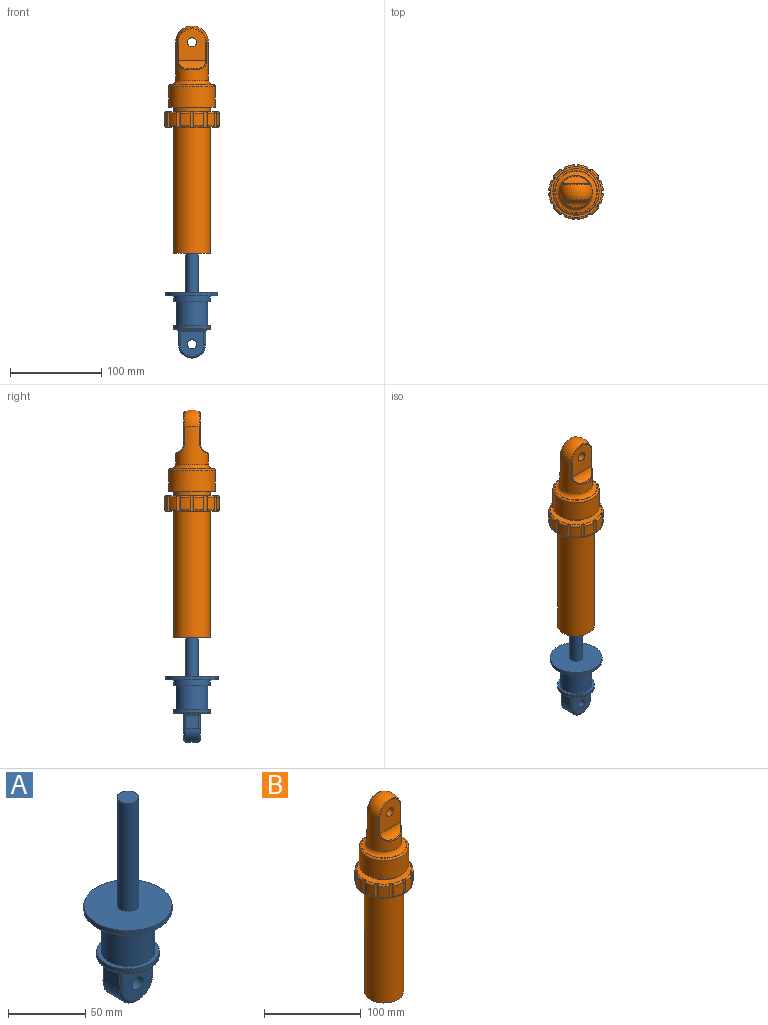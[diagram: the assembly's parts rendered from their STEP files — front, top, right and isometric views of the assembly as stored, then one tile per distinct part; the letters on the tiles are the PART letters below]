
ASSEMBLY  parts=2 mates=1
PART A: 32 faces, bbox 57.1x57.1x158.7 mm
  f0: plane 38.37x38.37mm, normal (0,0,-1), area 420.3mm2, adj f18,f21,f22,f25,f26,f28,f29,f30
  f1: plane 57.1x57.1mm, normal (0,0,1), area 2407mm2, adj f2,f16
  f2: cylinder r=28.55mm len=57.1mm, axis (0,0,-1), area 645.3mm2, adj f1,f3
  f3: plane 57.1x57.1mm, normal (0,0,-1), area 1281.1mm2, adj f2,f4
  f4: cylinder r=20.18mm len=40.37mm, axis (0,0,-1), area 815.9mm2, adj f3,f5
  f5: plane 40.37x40.37mm, normal (0,0,-1), area 322.7mm2, adj f4,f6
  f6: cylinder r=17.46mm len=34.91mm, axis (0,0,-1), area 2870.3mm2, adj f5,f7
  f7: plane 40.37x40.37mm, normal (0,0,1), area 322.7mm2, adj f6,f8
  f8: cylinder r=20.18mm len=40.37mm, axis (0,0,-1), area 424.7mm2, adj f7,f31
  f9: cylinder r=15.04mm len=30.07mm, axis (0,1,0), area 661.5mm2, adj f10,f11,f20,f23
  f10: plane 14.38x14mm, normal (1,0,0), area 201.3mm2, adj f9,f24,f27,f30
  f11: plane 14.38x14mm, normal (-1,0,0), area 201.3mm2, adj f9,f17,f18,f19
  f12: cylinder r=5.1mm len=18mm, axis (0,1,0), area 576.8mm2, adj f13,f14
  f13: plane 27.43x26.07mm, normal (0,-1,0), area 560.4mm2, adj f12,f17,f20,f24,f25
  f14: plane 27.43x26.07mm, normal (0,1,0), area 560.4mm2, adj f12,f19,f23,f26,f27
  f15: plane 14x14mm, normal (0,0,1), area 153.9mm2, adj f16
  f16: cylinder r=7mm len=85.45mm, axis (0,0,-1), area 3758.4mm2, adj f1,f15
  f17: cylinder r=2mm len=14.38mm, axis (0,0,1), area 45.2mm2, adj f11,f13,f20,f21
  f18: cylinder r=2mm len=14mm, axis (0,-1,0), area 44mm2, adj f0,f11,f21,f22
  f19: cylinder r=2mm len=14.38mm, axis (0,0,-1), area 45.2mm2, adj f11,f14,f22,f23
  f20: torus R=13.04mm, axis (0,-1,0), area 141.3mm2, adj f9,f13,f17,f24
  f21: torus R=4mm, axis (0,0,-1), area 13.5mm2, adj f0,f17,f18,f25
  f22: torus R=4mm, axis (0,0,-1), area 13.5mm2, adj f0,f18,f19,f26
  f23: torus R=13.04mm, axis (0,-1,0), area 141.3mm2, adj f9,f14,f19,f27
  f24: cylinder r=2mm len=14.38mm, axis (0,0,-1), area 45.2mm2, adj f10,f13,f20,f28
  f25: cylinder r=2mm len=26.07mm, axis (-1,0,0), area 81.9mm2, adj f0,f13,f21,f28
  f26: cylinder r=2mm len=26.07mm, axis (1,0,0), area 81.9mm2, adj f0,f14,f22,f29
  f27: cylinder r=2mm len=14.38mm, axis (0,0,1), area 45.2mm2, adj f10,f14,f23,f29
  f28: torus R=4mm, axis (0,0,-1), area 13.5mm2, adj f0,f24,f25,f30
  f29: torus R=4mm, axis (0,0,-1), area 13.5mm2, adj f0,f26,f27,f30
  f30: cylinder r=2mm len=14mm, axis (0,1,0), area 44mm2, adj f0,f10,f28,f29
  f31: torus R=19.18mm, axis (0,0,-1), area 195.6mm2, adj f0,f8
PART B: 75 faces, bbox 64.8x64.8x249.7 mm
  f0: cylinder r=29.95mm len=13.38mm, axis (0,0,-1), area 152.5mm2, adj f22,f51,f55,f66
  f1: cylinder r=29.95mm len=13.38mm, axis (0,0,-1), area 152.5mm2, adj f11,f23,f65,f66
  f2: cylinder r=29.95mm len=13.38mm, axis (0,0,-1), area 152.5mm2, adj f12,f24,f64,f65
  f3: cylinder r=29.95mm len=13.38mm, axis (0,0,-1), area 152.5mm2, adj f16,f25,f61,f63
  f4: cylinder r=29.95mm len=13.38mm, axis (0,0,-1), area 152.5mm2, adj f17,f26,f60,f62
  f5: cylinder r=29.95mm len=13.38mm, axis (0,0,-1), area 152.5mm2, adj f15,f27,f61,f62
  f6: cylinder r=29.95mm len=13.38mm, axis (0,0,-1), area 152.5mm2, adj f13,f28,f60,f64
  f7: cylinder r=29.95mm len=13.38mm, axis (0,0,-1), area 152.5mm2, adj f14,f29,f59,f63
  f8: cylinder r=29.95mm len=13.38mm, axis (0,0,-1), area 152.5mm2, adj f18,f30,f58,f59
  f9: cylinder r=29.95mm len=13.38mm, axis (0,0,-1), area 152.5mm2, adj f19,f31,f57,f58
  f10: cylinder r=29.95mm len=13.38mm, axis (0,0,-1), area 152.5mm2, adj f20,f32,f56,f57
  f11: torus R=27.95mm, axis (0,0,-1), area 41.4mm2, adj f1,f40,f65,f66
  f12: torus R=27.95mm, axis (0,0,-1), area 41.4mm2, adj f2,f40,f64,f65
  f13: torus R=27.95mm, axis (0,0,-1), area 41.4mm2, adj f6,f40,f60,f64
  f14: torus R=27.95mm, axis (0,0,-1), area 41.4mm2, adj f7,f40,f59,f63
  f15: torus R=27.95mm, axis (0,0,-1), area 41.4mm2, adj f5,f40,f61,f62
  f16: torus R=27.95mm, axis (0,0,-1), area 41.4mm2, adj f3,f40,f61,f63
  f17: torus R=27.95mm, axis (0,0,-1), area 41.4mm2, adj f4,f40,f60,f62
  f18: torus R=27.95mm, axis (0,0,-1), area 41.4mm2, adj f8,f40,f58,f59
  f19: torus R=27.95mm, axis (0,0,-1), area 41.4mm2, adj f9,f40,f57,f58
  f20: torus R=27.95mm, axis (0,0,-1), area 41.4mm2, adj f10,f40,f56,f57
  f21: torus R=27.95mm, axis (0,0,-1), area 41.4mm2, adj f40,f41,f55,f56
  f22: torus R=27.95mm, axis (0,0,1), area 41.4mm2, adj f0,f42,f55,f66
  f23: torus R=27.95mm, axis (0,0,1), area 41.4mm2, adj f1,f42,f65,f66
  f24: torus R=27.95mm, axis (0,0,1), area 41.4mm2, adj f2,f42,f64,f65
  f25: torus R=27.95mm, axis (0,0,1), area 41.4mm2, adj f3,f42,f61,f63
  f26: torus R=27.95mm, axis (0,0,1), area 41.4mm2, adj f4,f42,f60,f62
  f27: torus R=27.95mm, axis (0,0,1), area 41.4mm2, adj f5,f42,f61,f62
  f28: torus R=27.95mm, axis (0,0,1), area 41.4mm2, adj f6,f42,f60,f64
  f29: torus R=27.95mm, axis (0,0,1), area 41.4mm2, adj f7,f42,f59,f63
  f30: torus R=27.95mm, axis (0,0,1), area 41.4mm2, adj f8,f42,f58,f59
  f31: torus R=27.95mm, axis (0,0,1), area 41.4mm2, adj f9,f42,f57,f58
  f32: torus R=27.95mm, axis (0,0,1), area 41.4mm2, adj f10,f42,f56,f57
  f33: cylinder r=18mm len=41.42mm, axis (0,0,-1), area 2491.2mm2, adj f45,f49,f68,f69,f70,f72,f73,f74
  f34: plane 34.82x30mm, normal (0,1,0), area 866.2mm2, adj f46,f47,f71,f72,f73,f74
  f35: plane 34.82x30mm, normal (0,-1,0), area 866.2mm2, adj f46,f48,f67,f68,f69,f70
  f36: plane 46.85x46.85mm, normal (0,0,1), area 62.3mm2, adj f49,f50
  f37: cylinder r=25.43mm len=50.85mm, axis (0,0,-1), area 3675.4mm2, adj f38,f50
  f38: plane 50.85x50.85mm, normal (0,0,-1), area 751.3mm2, adj f37,f39
  f39: cylinder r=20.18mm len=40.37mm, axis (0,0,-1), area 584.3mm2, adj f38,f40
  f40: plane 55.91x55.91mm, normal (0,0,1), area 1175.2mm2, adj f11,f12,f13,f14,f15,f16,f17,f18
  f41: cylinder r=29.95mm len=13.38mm, axis (0,0,-1), area 152.5mm2, adj f21,f52,f55,f56
  f42: plane 55.91x55.91mm, normal (0,0,-1), area 1175.2mm2, adj f22,f23,f24,f25,f26,f27,f28,f29
  f43: cylinder r=20.18mm len=138.32mm, axis (0,0,-1), area 17541.3mm2, adj f42,f44
  f44: plane 40.37x40.37mm, normal (0,0,-1), area 1125.9mm2, adj f43,f53
  f45: sphere r=18mm, area 958mm2, adj f33,f67,f71
  f46: cylinder r=5.1mm len=18mm, axis (0,-1,0), area 576.8mm2, adj f34,f35
  f47: cylinder r=10.27mm len=30mm, axis (1,0,0), area 313.1mm2, adj f34,f74
  f48: cylinder r=10.27mm len=30mm, axis (1,0,0), area 313mm2, adj f35,f70
  f49: torus R=23mm, axis (0,0,1), area 977.9mm2, adj f33,f36
  f50: torus R=23.43mm, axis (0,0,1), area 487.6mm2, adj f36,f37
  f51: torus R=27.95mm, axis (0,0,-1), area 41.4mm2, adj f0,f40,f55,f66
  f52: torus R=27.95mm, axis (0,0,1), area 41.4mm2, adj f41,f42,f55,f56
  f53: cylinder r=7mm len=150mm, axis (0,0,-1), area 6597.3mm2, adj f44,f54
  f54: plane 14x14mm, normal (0,0,-1), area 153.9mm2, adj f53
  f55: cylinder r=2.15mm len=17.38mm, axis (0,0,1), area 96.9mm2, adj f0,f21,f22,f41,f51,f52
  f56: cylinder r=2.15mm len=17.38mm, axis (0,0,1), area 96.9mm2, adj f10,f20,f21,f32,f41,f52
  f57: cylinder r=2.15mm len=17.38mm, axis (0,0,1), area 96.9mm2, adj f9,f10,f19,f20,f31,f32
  f58: cylinder r=2.15mm len=17.38mm, axis (0,0,1), area 96.9mm2, adj f8,f9,f18,f19,f30,f31
  f59: cylinder r=2.15mm len=17.38mm, axis (0,0,1), area 96.9mm2, adj f7,f8,f14,f18,f29,f30
  f60: cylinder r=2.15mm len=17.38mm, axis (0,0,1), area 96.9mm2, adj f4,f6,f13,f17,f26,f28
  f61: cylinder r=2.15mm len=17.38mm, axis (0,0,1), area 96.9mm2, adj f3,f5,f15,f16,f25,f27
  f62: cylinder r=2.15mm len=17.38mm, axis (0,0,1), area 96.9mm2, adj f4,f5,f15,f17,f26,f27
  f63: cylinder r=2.15mm len=17.38mm, axis (0,0,1), area 96.9mm2, adj f3,f7,f14,f16,f25,f29
  f64: cylinder r=2.15mm len=17.38mm, axis (0,0,1), area 96.9mm2, adj f2,f6,f12,f13,f24,f28
  f65: cylinder r=2.15mm len=17.38mm, axis (0,0,1), area 96.9mm2, adj f1,f2,f11,f12,f23,f24
  f66: cylinder r=2.15mm len=17.38mm, axis (0,0,1), area 96.9mm2, adj f0,f1,f11,f22,f23,f51
  f67: torus R=15mm, axis (0,1,0), area 52.6mm2, adj f35,f45,f68,f69
  f68: cylinder r=1mm len=19.86mm, axis (0,0,-1), area 21.4mm2, adj f33,f35,f67,f70
  f69: cylinder r=1mm len=19.86mm, axis (0,0,-1), area 21.4mm2, adj f33,f35,f67,f70
  f70: bspline ~31.81x10.73mm, area 55.2mm2, adj f33,f35,f48,f68,f69
  f71: torus R=15mm, axis (0,1,0), area 52.6mm2, adj f34,f45,f72,f73
  f72: cylinder r=1mm len=19.86mm, axis (0,0,-1), area 21.4mm2, adj f33,f34,f71,f74
  f73: cylinder r=1mm len=19.86mm, axis (0,0,-1), area 21.4mm2, adj f33,f34,f71,f74
  f74: bspline ~31.81x10.85mm, area 55.2mm2, adj f33,f34,f47,f72,f73
PLACE A t=(0,0,-119)mm
PLACE B t=(0,0,-161.73)mm
MATE cylindrical B.f53 <-> A.f16  axis (0,0,-1) through (0,0,-193.9)mm
